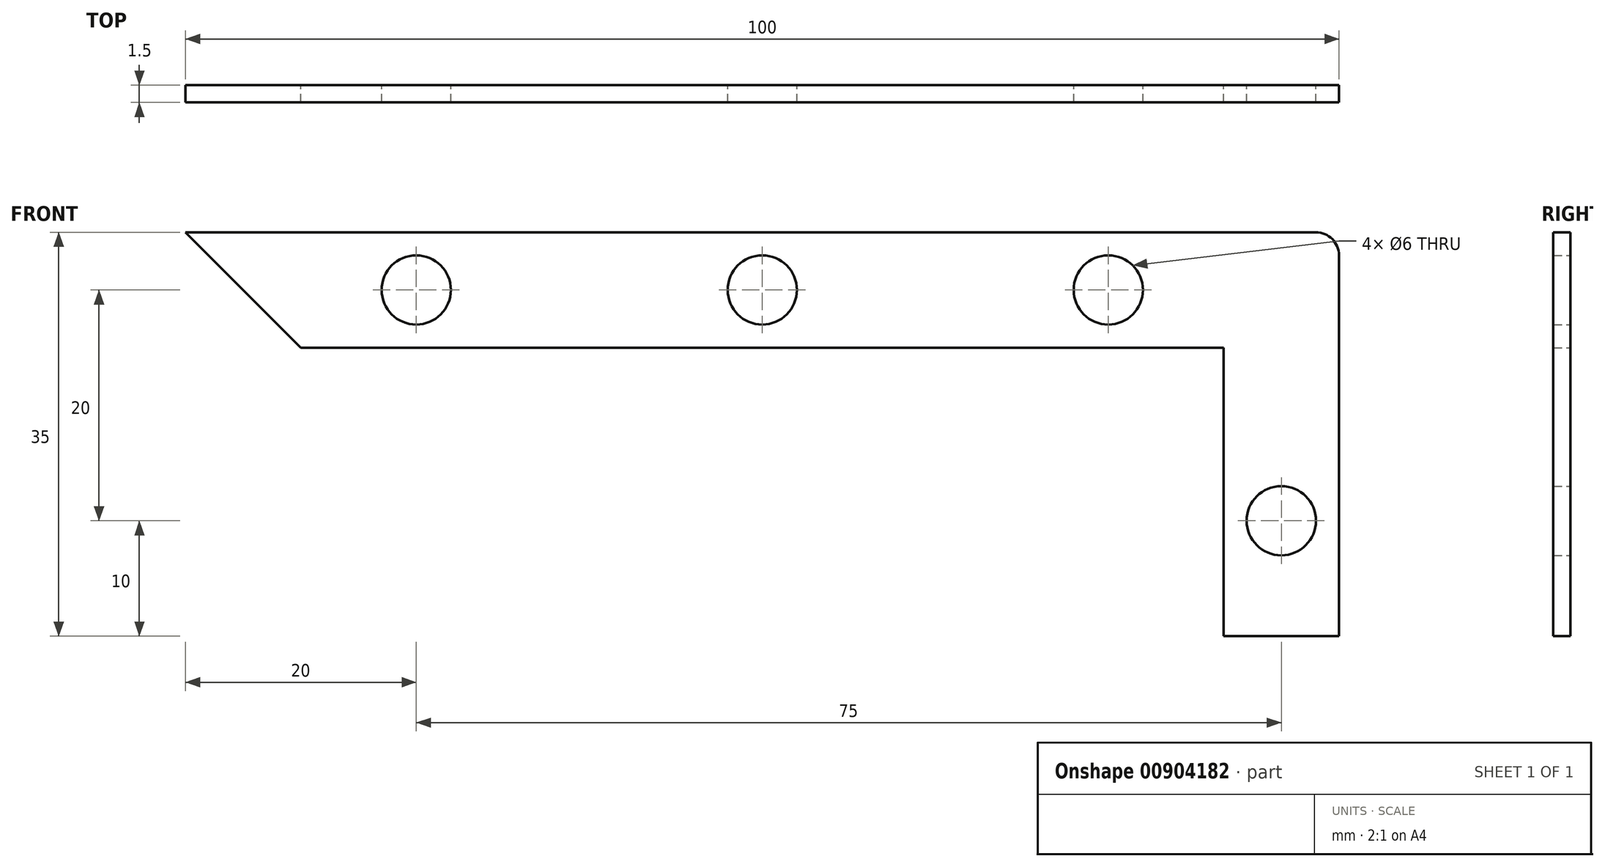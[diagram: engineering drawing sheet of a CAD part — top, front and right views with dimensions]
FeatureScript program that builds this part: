
annotation { "Feature Type Name" : "Feature", "Feature Type Description" : "" }
export const myFeature = defineFeature(function(context is Context, id is Id, definition is map)
    precondition{}
    {
        {
            var Q0;
            Q0=qCreatedBy(makeId("Front.planeOp"),FACE);
            var sketch = newSketch(context, id + "F0", { "sketchPlane" : qUnion([Q0])});
            skLineSegment(sketch, "E0.top", {"start": v(40, -19) * mm, "end": v(50, -19) * mm});
            skLineSegment(sketch, "E0.right", {"start": v(50, 14) * mm, "end": v(50, -19) * mm});
            skPoint(sketch, "E0.middle", {"position": v(0, 0) * mm});
            skPoint(sketch, "E1", {"position": v(-50, 16) * mm});
            skPoint(sketch, "E2", {"position": v(-40, 6) * mm});
            skLineSegment(sketch, "E3", {"start": v(-50, 16) * mm, "end": v(-40, 6) * mm});
            skPoint(sketch, "E4", {"position": v(48, 14) * mm});
            skArc(sketch, "E5", {"start": v(50, 14) * mm, "mid": v(49.41, 15.41) * mm, "end": v(48, 16) * mm});
            skPoint(sketch, "E6", {"position": v(-30, 11) * mm});
            skPoint(sketch, "E7", {"position": v(0, 11) * mm});
            skPoint(sketch, "E8", {"position": v(30, 11) * mm});
            skCircle(sketch, "E9", {"center": v(-30, 11) * mm, "radius": 3 * mm});
            skCircle(sketch, "E10", {"center": v(0, 11) * mm, "radius": 3 * mm});
            skCircle(sketch, "E11", {"center": v(30, 11) * mm, "radius": 3 * mm});
            skPoint(sketch, "E12", {"position": v(45, -9) * mm});
            skCircle(sketch, "E13", {"center": v(45, -9) * mm, "radius": 3 * mm});
            skLineSegment(sketch, "E14.bottom", {"start": v(-40, 6) * mm, "end": v(40, 6) * mm});
            skLineSegment(sketch, "E14.right", {"start": v(40, 6) * mm, "end": v(40, -19) * mm});
            skLineSegment(sketch, "E15", {"start": v(-50, 16) * mm, "end": v(48, 16) * mm});
            skSolve(sketch);
        }
        {
            var Q0;
            Q0=qSketchRegion(id+"F0",true);
            extrude(context, id + "F1", {"entities" : qUnion([Q0]), "depth" : 1.5 * mm, "offsetDistance" : 25 * mm});
        }
    });
